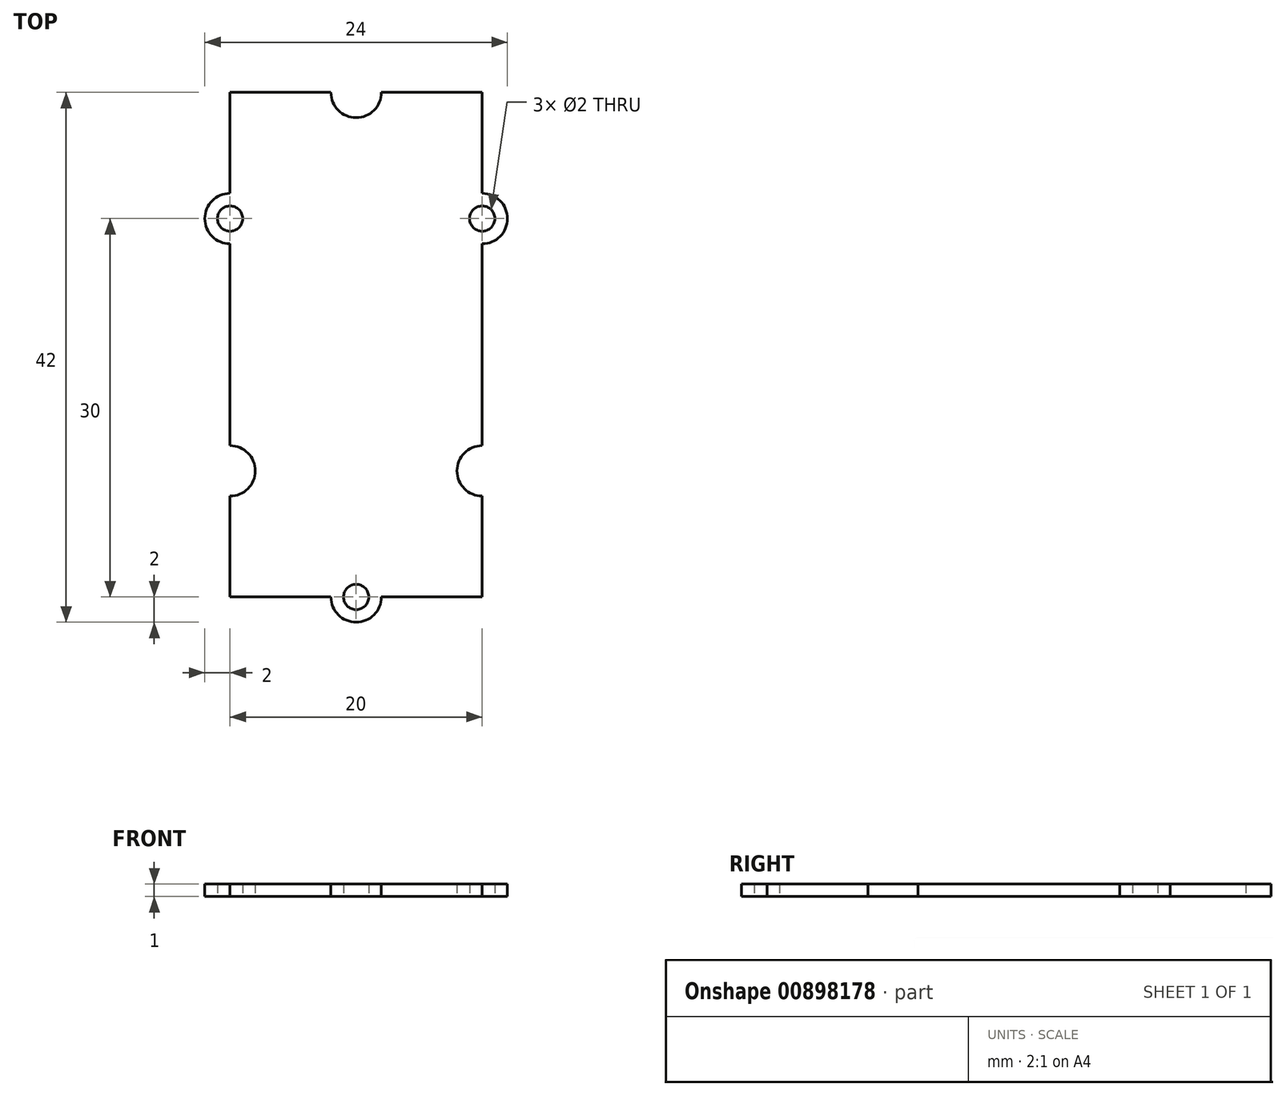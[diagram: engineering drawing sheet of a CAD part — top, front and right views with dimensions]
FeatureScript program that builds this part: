
annotation { "Feature Type Name" : "Feature", "Feature Type Description" : "" }
export const myFeature = defineFeature(function(context is Context, id is Id, definition is map)
    precondition{}
    {
        {
            var Q0;
            Q0=qCreatedBy(makeId("Top.planeOp"),FACE);
            var sketch = newSketch(context, id + "F0", { "sketchPlane" : qUnion([Q0])});
            skLineSegment(sketch, "E0.bottom", {"start": v(10, 20) * mm, "end": v(-10, 20) * mm});
            skLineSegment(sketch, "E0.top", {"start": v(10, -20) * mm, "end": v(-10, -20) * mm});
            skLineSegment(sketch, "E0.left", {"start": v(10, 20) * mm, "end": v(10, -20) * mm});
            skLineSegment(sketch, "E0.right", {"start": v(-10, 20) * mm, "end": v(-10, -20) * mm});
            skPoint(sketch, "E0.middle", {"position": v(0, 0) * mm});
            skPoint(sketch, "E1", {"position": v(0, 20) * mm});
            skPoint(sketch, "E2", {"position": v(0, -20) * mm});
            skPoint(sketch, "E3", {"position": v(10, -10) * mm});
            skPoint(sketch, "E4", {"position": v(10, 10) * mm});
            skPoint(sketch, "E5", {"position": v(-10, 10) * mm});
            skPoint(sketch, "E6", {"position": v(-10, -10) * mm});
            skCircle(sketch, "E7", {"center": v(0, 20) * mm, "radius": 2 * mm});
            skCircle(sketch, "E8", {"center": v(-10, -10) * mm, "radius": 2 * mm});
            skCircle(sketch, "E9", {"center": v(10, -10) * mm, "radius": 2 * mm});
            skArc(sketch, "E10", {"start": v(-10, 8) * mm, "mid": v(-12, 10) * mm, "end": v(-10, 12) * mm});
            skArc(sketch, "E11", {"start": v(10, 8) * mm, "mid": v(12, 10) * mm, "end": v(10, 12) * mm});
            skArc(sketch, "E12", {"start": v(-2, -20) * mm, "mid": v(0, -22) * mm, "end": v(2, -20) * mm});
            skSolve(sketch);
        }
        {
            var Q0;
            Q0 = qSketchRegion(id + "F0", true);
            extrude(context, id + "F1", {"entities" : qUnion([Q0]), "depth" : 1 * mm, "offsetDistance" : 25 * mm});
        }
        {
            var Q0;
            Q0=sQuery(id+"F0.wireOp",VERTEX,"E1");
            var Q1;
            Q1=sQuery(id+"F0.wireOp",VERTEX,"E6");
            var Q2;
            Q2=sQuery(id+"F0.wireOp",VERTEX,"E3");
            var Q3;
            Q3=makeQuery(id+"F1.opExtrude","SWEPT_BODY",BODY,{"disambiguationData":[OSD([sQuery(id+"F0.wireOp",EDGE,"E0.bottom"),sQuery(id+"F0.wireOp",EDGE,"E0.top"),sQuery(id+"F0.wireOp",EDGE,"E0.left"),sQuery(id+"F0.wireOp",EDGE,"E0.right"),sQuery(id+"F0.wireOp",EDGE,"E7"),sQuery(id+"F0.wireOp",EDGE,"E8"),sQuery(id+"F0.wireOp",EDGE,"E9"),sQuery(id+"F0.wireOp",EDGE,"E10"),sQuery(id+"F0.wireOp",EDGE,"E11"),sQuery(id+"F0.wireOp",EDGE,"E12")])]});
            hole(context, id + "F2", {"style" : HoleStyle.SIMPLE, "endStyle" : HoleEndStyle.THROUGH, "oppositeDirection" : true, "holeDiameter" : 4 * mm, "majorDiameter" : 5 * mm, "tappedDepth" : 12 * mm, "tapClearance" : 3, "locations" : qUnion([Q0, Q1, Q2]), "scope" : qUnion([Q3])});
        }
        {
            var Q0;
            Q0=sQuery(id+"F0.wireOp",VERTEX,"E5");
            var Q1;
            Q1=sQuery(id+"F0.wireOp",VERTEX,"E4");
            var Q2;
            Q2=sQuery(id+"F0.wireOp",VERTEX,"E2");
            var Q3;
            Q3=makeQuery(id+"F1.opExtrude","SWEPT_BODY",BODY,{"disambiguationData":[OSD([sQuery(id+"F0.wireOp",EDGE,"E0.bottom"),sQuery(id+"F0.wireOp",EDGE,"E0.top"),sQuery(id+"F0.wireOp",EDGE,"E0.left"),sQuery(id+"F0.wireOp",EDGE,"E0.right"),sQuery(id+"F0.wireOp",EDGE,"E7"),sQuery(id+"F0.wireOp",EDGE,"E8"),sQuery(id+"F0.wireOp",EDGE,"E9"),sQuery(id+"F0.wireOp",EDGE,"E10"),sQuery(id+"F0.wireOp",EDGE,"E11"),sQuery(id+"F0.wireOp",EDGE,"E12")])]});
            hole(context, id + "F3", {"style" : HoleStyle.SIMPLE, "endStyle" : HoleEndStyle.THROUGH, "oppositeDirection" : true, "holeDiameter" : 2 * mm, "majorDiameter" : 5 * mm, "tappedDepth" : 12 * mm, "tapClearance" : 3, "locations" : qUnion([Q0, Q1, Q2]), "scope" : qUnion([Q3])});
        }
    });
